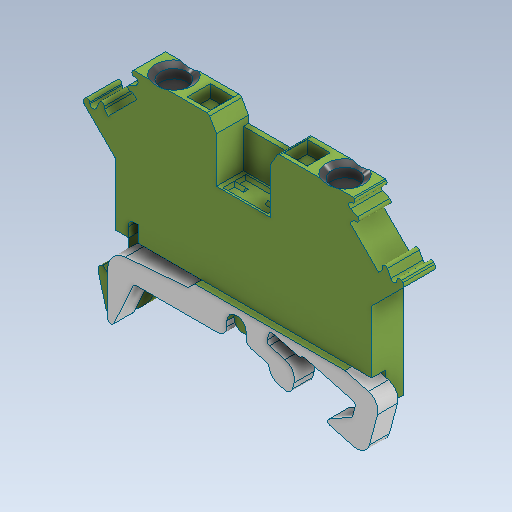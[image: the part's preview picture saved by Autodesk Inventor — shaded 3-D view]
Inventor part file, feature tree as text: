
AUTODESK INVENTOR PART (.ipt)
format: ipt  version: 2025.2 (Build 292293000, 293)  size: 841,216 bytes
history: native  units: mm
features: other x130, sketch x12, extrude x10, hole x2
ambient origin geometry x8: Origin, YZ Plane, XZ Plane, XY Plane, X Axis, Y Axis, Z Axis, Center Point
bodies: Solid1 (feature_tree)
feature tree (154):
  extrude  "Extrusion1"  Depth=2.1mm TaperAngle=0.0deg
  extrude  "Extrusion2"  Depth=2.0mm TaperAngle=0.0deg
  extrude  "Extrusion3"  Depth=7.0mm TaperAngle=0.0deg
  extrude  "Extrusion4"  Depth=5.0mm TaperAngle=0.0deg
  extrude  "Extrusion5"  Depth=3.6mm TaperAngle=0.0deg
  extrude  "Extrusion6"  TaperAngle=0.0deg  [1 undecoded]
  extrude  "Extrusion7"  TaperAngle=0.0deg  [1 undecoded]
  extrude  "Extrusion8"  TaperAngle=0.0deg  [1 undecoded]
  hole  "Hole1"  [1 undecoded]
  hole  "Hole2"  [1 undecoded]
  extrude  "Extrusion9"  Depth=10.0mm
  extrude  "Extrusion10"  Depth=10.0mm
  other  "1_2_XY"
  other  "1_2_YZ"
  other  "1_2_ZX"
  other  "1_2_X"
  other  "1_2_Y"
  other  "1_2_Z"
  other  "1_2_Center"
  other  "1_3_XY"
  other  "1_3_YZ"
  other  "1_3_ZX"
  other  "1_3_X"
  other  "1_3_Y"
  other  "1_3_Z"
  other  "1_3_Center"
  other  "1_4_XY"
  other  "1_4_YZ"
  other  "1_4_ZX"
  other  "1_4_X"
  other  "1_4_Y"
  other  "1_4_Z"
  other  "1_4_Center"
  other  "1_5_XY"
  other  "1_5_YZ"
  other  "1_5_ZX"
  other  "1_5_X"
  other  "1_5_Y"
  other  "1_5_Z"
  other  "1_5_Center"
  other  "1_6_XY"
  other  "1_6_YZ"
  other  "1_6_ZX"
  other  "1_6_X"
  other  "1_6_Y"
  other  "1_6_Z"
  other  "1_6_Center"
  other  "1_7_XY"
  other  "1_7_YZ"
  other  "1_7_ZX"
  other  "1_7_X"
  other  "1_7_Y"
  other  "1_7_Z"
  other  "1_7_Center"
  other  "1_8_XY"
  other  "1_8_YZ"
  other  "1_8_ZX"
  other  "1_8_X"
  other  "1_8_Y"
  other  "1_8_Z"
  other  "1_8_Center"
  other  "MD_XY"
  other  "MD_YZ"
  other  "MD_ZX"
  other  "MD_X"
  other  "MD_Y"
  other  "MD_Z"
  other  "MD_Center"
  other  "OP_XY"
  other  "OP_YZ"
  other  "OP_ZX"
  other  "OP_X"
  other  "OP_Y"
  other  "OP_Z"
  other  "OP_Center"
  other  "a1_XY"
  other  "a1_YZ"
  other  "a1_ZX"
  other  "a1_X"
  other  "a1_Y"
  other  "a1_Z"
  other  "a1_Center"
  other  "b2_XY"
  other  "b2_YZ"
  other  "b2_ZX"
  other  "b2_X"
  other  "b2_Y"
  other  "b2_Z"
  other  "b2_Center"
  other  "j3_XY"
  other  "j3_YZ"
  other  "j3_ZX"
  other  "j3_X"
  other  "j3_Y"
  other  "j3_Z"
  other  "j3_Center"
  other  "m4_XY"
  other  "m4_YZ"
  other  "m4_ZX"
  other  "m4_X"
  other  "m4_Y"
  other  "m4_Z"
  other  "m4_Center"
  other  "m5_XY"
  other  "m5_YZ"
  other  "m5_ZX"
  other  "m5_X"
  other  "m5_Y"
  other  "m5_Z"
  other  "m5_Center"
  other  "z6_XY"
  other  "z6_YZ"
  other  "z6_ZX"
  other  "z6_X"
  other  "z6_Y"
  other  "z6_Z"
  other  "z6_Center"
  other  "z7_XY"
  other  "z7_YZ"
  other  "z7_ZX"
  other  "z7_X"
  other  "z7_Y"
  other  "z7_Z"
  other  "z7_Center"
  other  "Edição direta1"
  other  "Edição direta2"
  other  "Edição direta3"
  other  "Edição direta4"
  other  "Edição direta5"
  other  "Edição direta6"
  other  "Edição direta7"
  other  "Edição direta8"
  other  "Edição direta9"
  sketch  "Skizze_1"  dims[d0=5.0mm d1=0.0mm d2=2.1mm d3=0.0mm]
  sketch  "Skizze_14"  dims[d39=0.0mm d40=0.0mm]
  sketch  "Skizze_15"  dims[d41=3.0mm d42=10.0mm d43=10.0mm d44=12.3mm d45=10.0mm d46=10.0mm]
  sketch  "Skizze_16"  dims[d47=12.0mm d48=10.0mm d49=10.0mm d50=0.25mm d51=0.55mm d52=-0.36mm d53=-0.4mm d54=0.0mm d55=0.0mm d56=0.0mm d57=0.0mm d58=0.35mm d59=0.5mm]
  sketch  "Skizze_2"  dims[d4=2.1mm d5=0.0mm d6=2.0mm d7=0.0mm]
  sketch  "Skizze_3"  dims[d8=0.8mm d9=0.0mm d10=7.0mm d11=0.0mm]
  sketch  "Skizze_4"  dims[d12=3.4mm d13=0.0mm d14=5.0mm d15=0.0mm]
  sketch  "Skizze_5"  dims[d16=4.2mm d17=6.0mm d18=5.8mm d19=2.0mm d20=18.545904mm d21=2.0mm d22=0.0mm]
  sketch  "Sketch9"  dims[d32=3.6mm d33=0.0mm d34=0.0mm]
  sketch  "Sketch10"  dims[d37=0.0mm d38=0.0mm]
  sketch  "Skizze_8"  dims[d23=4.2mm d24=6.0mm d25=5.8mm d26=2.0mm d27=18.545904mm d28=2.0mm d29=0.0mm d30=3.6mm d31=0.0mm]
  sketch  "Skizze_9"  dims[d35=0.0mm d36=0.0mm]
  other  "Escala1"
  other  "Escala2"
  other  "Escala3"
  other  "Tamanho1"
  other  "Tamanho2"
  other  "Tamanho3"
  other  "Mover1"
  other  "Mover2"
  other  "Tamanho4"
note: 5 required parameter values undecoded (feature->parameter linkage not recoverable at this tier; creation-order binding heuristic only, values carry confidence <= 0.55)
